# Revit family: Reduced Couplings-Zurn_Wilkins-FP23 (112x114_8x6_inch)
name_source: partatom
category: Pipe Accessories
units: mm (PartAtom-declared; Revit-internal decimal feet)

## family parameters
Always vertical = Yes
Cut with Voids When Loaded = No
OmniClass Number = 23.65.55.14.11
OmniClass Title = Inlet/Outlet Valves for Liquid Services
Part Type = Valve - Breaks Into
Round Connector Dimension = Use Radius
Shared = No
Work Plane-Based = No

## types (13) — shared parameters
Assembly Code = D2020300
Default Elevation = 0' - 0"
Description = REDUCING COUPLINGS
Flow Rate (GPM) = 0 GPM
Height = 1' - 0"
Hydrostatic Test Pressure = 0.00 psi
Length = 2' - 0"
Main Material = Paint - Zurn - Ductile Iron Red
Manufacturer = Zurn Water, LLC
Manufacturer Brand = Zurn Wilkins
Max Working Water Pressure = 300.00 psi
Max Working Water Temperature = 0 °F
Modified Date = 10/15/25
Product Documentation Link = https://files.zurn.com
Product Installation Sheet URL = https://files.zurn.com
Product Page URL = https://www.zurn.com
Product data URL = https://www.bimobject.com
URL = https://www.zurn.com
Width = 1' - 0"

## per-type parameters (varying)
| type | D | DIM A | DIM B | DIM C | E | F | G | H | I | IN PORTION | J | K | L | Model | Nominal Diameter | Nominal Radius | Product Weight (lbs) |
| 3X212-FP23 (3" X 2 1/2" -FP23) | 0' - 1 1/2" | 0' - 6 15/32" | 0' - 4 23/32" | 0' - 1 29/32" | 0' - 3 1/2" | 0' - 0 3/4" | 0' - 1 3/32" | 0' - 0 13/32" | 0' - 0 3/4" | Reduced couplings-Zurn_Wilkins-FP23_IN_(114-8_Inch) : 3 X 2 1/2 | 0' - 0 9/32" | 0' - 0 1/4" | 0' - 0 3/16" | 3X212-FP23 | 0' - 3" | 0' - 1 1/2" | 3 |
| 112X114-FP23 (1 1/2" X 1 1/4" -FP23) | 0' - 0 13/16" | 0' - 4 9/16" | 0' - 2 7/8" | 0' - 1 25/32" | 0' - 2 3/16" | 0' - 0 19/32" | 0' - 0 1/2" | 0' - 0 11/32" | 0' - 0 19/32" | Reduced couplings-Zurn_Wilkins-FP23_IN_(114-8_Inch) : 1 1/2 X 1 1/4 | 0' - 0 3/16" | 0' - 0 1/4" | 0' - 0 1/8" | 112X114-FP23 | 0' - 1 1/2" | 0' - 0 3/4" | 1 |
| 2X112-FP23 (2" X 1 1/2" -FP23) | 0' - 1" | 0' - 5 3/32" | 0' - 3 11/32" | 0' - 1 27/32" | 0' - 2 1/2" | 0' - 0 19/32" | 0' - 0 19/32" | 0' - 0 11/32" | 0' - 0 19/32" | Reduced couplings-Zurn_Wilkins-FP23_IN_(114-8_Inch) : 2 X 1 1/2 | 0' - 0 3/16" | 0' - 0 1/4" | 0' - 0 1/8" | 2X112-FP23 | 0' - 2" | 0' - 1" | 2 |
| 212X112-FP23 (2 1/2" X 1 1/2" -FP23) | 0' - 1 5/16" | 0' - 5 13/32" | 0' - 3 31/32" | 0' - 1 29/32" | 0' - 3" | 0' - 0 19/32" | 0' - 0 29/32" | 0' - 0 11/32" | 0' - 0 19/32" | Reduced couplings-Zurn_Wilkins-FP23_IN_(114-8_Inch) : 2 1/2 X 1 1/2 | 0' - 0 3/16" | 0' - 0 1/4" | 0' - 0 1/8" | 212X112-FP23 | 0' - 2 1/2" | 0' - 1 1/4" | 3 |
| 4X3-FP23 (4" X 3" -FP23) | 0' - 2" | 0' - 7 5/8" | 0' - 5 29/32" | 0' - 1 15/16" | 0' - 4 3/16" | 0' - 0 13/16" | 0' - 1 1/2" | 0' - 0 7/16" | 0' - 0 3/4" | Reduced couplings-Zurn_Wilkins-FP23_IN_(114-8_Inch) : 4 X 3 | 0' - 0 9/32" | 0' - 0 1/4" | 0' - 0 3/16" | 4X3-FP23 | 0' - 4" | 0' - 2" | 4 |
| 8X6-FP23 (8" X 6" -FP23) | 0' - 4" | 1' - 0 9/16" | 0' - 10 13/32" | 0' - 2 3/8" | 0' - 8" | 0' - 1 3/16" | 0' - 3 1/2" | 0' - 0 11/16" | 0' - 1 3/32" | Reduced couplings-Zurn_Wilkins-FP23_IN_(114-8_Inch) : 8 X 6 | 0' - 0 7/16" | 0' - 0 13/32" | 0' - 0 3/16" | 8X6-FP23 | 0' - 8" | 0' - 4" | 15 |
| 4X212-FP23 (4" X 2 1/2" -FP23) | 0' - 2" | 0' - 7 5/8" | 0' - 5 29/32" | 0' - 1 15/16" | 0' - 4 3/16" | 0' - 0 13/16" | 0' - 1 1/2" | 0' - 0 7/16" | 0' - 0 3/4" | Reduced couplings-Zurn_Wilkins-FP23_IN_(114-8_Inch) : 4 X 2 1/2 | 0' - 0 9/32" | 0' - 0 1/4" | 0' - 0 3/16" | 4X21/2-FP23 | 0' - 4" | 0' - 2" | 4 |
| 4X2-FP23 (4" X 2" -FP23) | 0' - 2" | 0' - 7 5/8" | 0' - 5 29/32" | 0' - 1 15/16" | 0' - 4 3/16" | 0' - 0 13/16" | 0' - 1 1/2" | 0' - 0 7/16" | 0' - 0 3/4" | Reduced couplings-Zurn_Wilkins-FP23_IN_(114-8_Inch) : 4 X 2 | 0' - 0 9/32" | 0' - 0 1/4" | 0' - 0 3/16" | 4X2-FP23 | 0' - 4" | 0' - 2" | 5 |
| 3X2-FP23 (3" X 2" -FP23) | 0' - 1 1/2" | 0' - 6 15/32" | 0' - 4 23/32" | 0' - 1 29/32" | 0' - 3 1/2" | 0' - 0 3/4" | 0' - 1 3/32" | 0' - 0 13/32" | 0' - 0 3/4" | Reduced couplings-Zurn_Wilkins-FP23_IN_(114-8_Inch) : 3 X 2 | 0' - 0 9/32" | 0' - 0 1/4" | 0' - 0 3/16" | 3X2-FP23 | 0' - 3" | 0' - 1 1/2" | 3 |
| 212X2-FP23 (2 1/2" X 2" -FP23) | 0' - 1 5/16" | 0' - 5 13/32" | 0' - 3 31/32" | 0' - 1 29/32" | 0' - 3" | 0' - 0 19/32" | 0' - 0 29/32" | 0' - 0 11/32" | 0' - 0 19/32" | Reduced couplings-Zurn_Wilkins-FP23_IN_(114-8_Inch) : 2 1/2 X 2 | 0' - 0 3/16" | 0' - 0 1/4" | 0' - 0 1/8" | 212X2-FP23 | 0' - 2 1/2" | 0' - 1 1/4" | 2 |
| 3X112-FP23 (3" X 1 1/2" -FP23) | 0' - 1 1/2" | 0' - 6 15/32" | 0' - 4 23/32" | 0' - 1 29/32" | 0' - 3 1/2" | 0' - 0 3/4" | 0' - 1 3/32" | 0' - 0 13/32" | 0' - 0 3/4" | Reduced couplings-Zurn_Wilkins-FP23_IN_(114-8_Inch) : 3 X 1 1/2 | 0' - 0 9/32" | 0' - 0 1/4" | 0' - 0 3/16" | 3X112-FP23 | 0' - 3" | 0' - 1 1/2" | 4 |
| 6X4-FP23 (6" X 4" -FP23) | 0' - 2" | 0' - 9 1/4" | 0' - 7 31/32" | 0' - 1 31/32" | 0' - 6" | 0' - 0 19/32" | 0' - 1 1/2" | 0' - 0 5/16" | 0' - 0 1/2" | Reduced couplings-Zurn_Wilkins-FP23_IN_(114-8_Inch) : 6 X 4 | 0' - 0 9/32" | 0' - 0 1/4" | 0' - 0 3/32" | 6X4-FP23 | 0' - 6" | 0' - 3" | 7 |
| 6X3-FP23 (6" X 3"-FP23) | 0' - 2" | 0' - 9 1/4" | 0' - 7 31/32" | 0' - 1 31/32" | 0' - 6" | 0' - 0 19/32" | 0' - 1 1/2" | 0' - 0 5/16" | 0' - 0 1/2" | Reduced couplings-Zurn_Wilkins-FP23_IN_(114-8_Inch) : 6 X 3 | 0' - 0 9/32" | 0' - 0 1/4" | 0' - 0 3/32" | 6X3-FP23 | 0' - 6" | 0' - 3" | 8 |

## geometry (parser evidence)
native form markers: Sweep x5
no freeform markers — native parametric forms only
